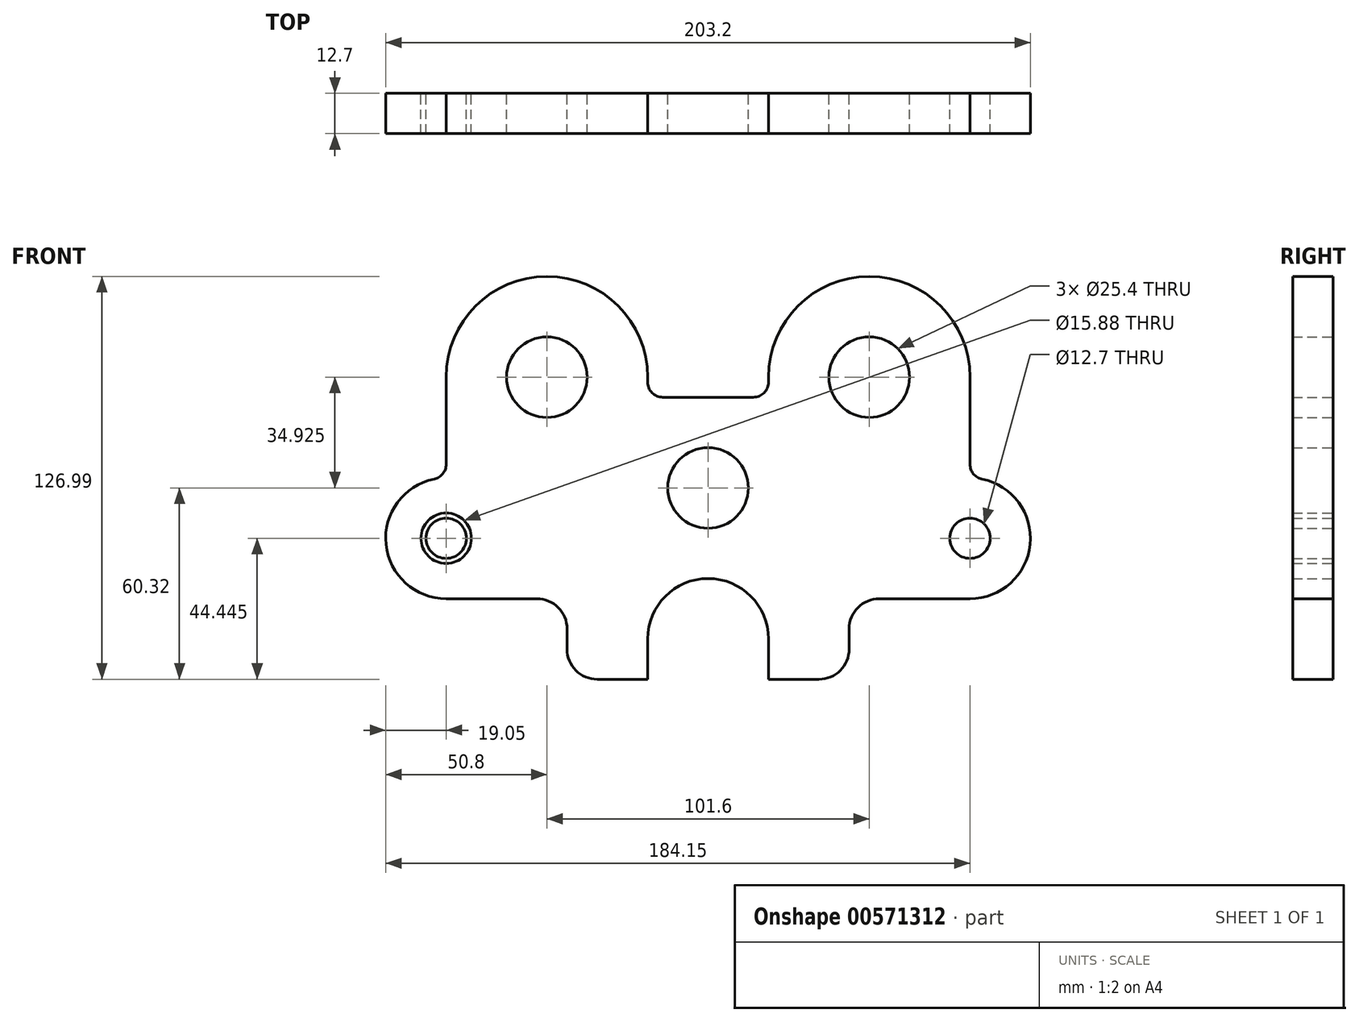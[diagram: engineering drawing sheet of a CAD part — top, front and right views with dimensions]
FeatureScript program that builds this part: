
annotation { "Feature Type Name" : "Feature", "Feature Type Description" : "" }
export const myFeature = defineFeature(function(context is Context, id is Id, definition is map)
    precondition{}
    {
        {
            var Q0;
            Q0=qCreatedBy(makeId("Front.planeOp"),FACE);
            var sketch = newSketch(context, id + "F0", { "sketchPlane" : qUnion([Q0])});
            skLineSegment(sketch, "E0", {"start": v(0, 76.7) * mm, "end": v(0, -75.9) * mm, "construction": true});
            skLineSegment(sketch, "E1", {"start": v(50.8, 76.08) * mm, "end": v(50.8, 12.52) * mm, "construction": true});
            skCircle(sketch, "E2", {"center": v(0, 0) * mm, "radius": 12.7 * mm});
            skCircle(sketch, "E3", {"center": v(50.8, 34.93) * mm, "radius": 12.7 * mm});
            skLineSegment(sketch, "E4", {"start": v(0, 28.58) * mm, "end": v(14.29, 28.58) * mm});
            skArc(sketch, "E5", {"start": v(82.55, 34.93) * mm, "mid": v(50.8, 66.68) * mm, "end": v(19.05, 34.93) * mm});
            skPoint(sketch, "E6.visualSharp", {"position": v(19.7, 28.58) * mm});
            skLineSegment(sketch, "E7", {"start": v(82.55, -34.92) * mm, "end": v(53.98, -34.92) * mm});
            skLineSegment(sketch, "E8", {"start": v(-29.42, 0) * mm, "end": v(25.25, 0) * mm, "construction": true});
            skCircle(sketch, "E9", {"center": v(82.55, -15.87) * mm, "radius": 6.35 * mm});
            skLineSegment(sketch, "E10", {"start": v(19.05, 34.93) * mm, "end": v(19.05, 33.34) * mm});
            skLineSegment(sketch, "E11", {"start": v(82.55, -7.94) * mm, "end": v(82.55, -31.6) * mm, "construction": true});
            skLineSegment(sketch, "E12", {"start": v(82.55, 34.93) * mm, "end": v(82.55, 7.46) * mm});
            skLineSegment(sketch, "E13", {"start": v(22.13, 34.93) * mm, "end": v(67.82, 34.93) * mm, "construction": true});
            skLineSegment(sketch, "E14", {"start": v(59.23, -15.87) * mm, "end": v(95.93, -15.87) * mm, "construction": true});
            skLineSegment(sketch, "E15", {"start": v(44.45, -44.45) * mm, "end": v(44.45, -50.8) * mm});
            skLineSegment(sketch, "E16", {"start": v(34.93, -60.32) * mm, "end": v(19.05, -60.32) * mm});
            skLineSegment(sketch, "E17", {"start": v(19.05, -60.32) * mm, "end": v(19.05, -47.62) * mm});
            skLineSegment(sketch, "E18.MirrorCS", {"start": v(0, 28.58) * mm, "end": v(-14.29, 28.58) * mm});
            skLineSegment(sketch, "E19.MirrorCS", {"start": v(-19.05, 34.93) * mm, "end": v(-19.05, 33.34) * mm});
            skArc(sketch, "E20.MirrorCS", {"start": v(-82.55, 34.93) * mm, "mid": v(-50.8, 66.68) * mm, "end": v(-19.05, 34.93) * mm});
            skLineSegment(sketch, "E21.MirrorCS", {"start": v(-82.55, 34.93) * mm, "end": v(-82.55, 7.46) * mm});
            skArc(sketch, "E22.MirrorCS", {"start": v(-82.55, -34.93) * mm, "mid": v(-101.5, -17.79) * mm, "end": v(-86.36, 2.8) * mm});
            skLineSegment(sketch, "E23.MirrorCS", {"start": v(-82.55, -34.93) * mm, "end": v(-53.97, -34.93) * mm});
            skLineSegment(sketch, "E24.MirrorCS", {"start": v(-44.45, -44.45) * mm, "end": v(-44.45, -50.8) * mm});
            skLineSegment(sketch, "E25.MirrorCS", {"start": v(-34.92, -60.32) * mm, "end": v(-19.05, -60.32) * mm});
            skLineSegment(sketch, "E26.MirrorCS", {"start": v(-19.05, -60.32) * mm, "end": v(-19.05, -47.62) * mm});
            skCircle(sketch, "E27.MirrorC", {"center": v(-50.8, 34.93) * mm, "radius": 12.7 * mm});
            skCircle(sketch, "E28.MirrorC", {"center": v(-82.55, -15.88) * mm, "radius": 6.35 * mm});
            skLineSegment(sketch, "E29.MirrorCS", {"start": v(-59.23, -15.87) * mm, "end": v(-95.93, -15.87) * mm, "construction": true});
            skLineSegment(sketch, "E30.MirrorCS", {"start": v(-82.55, -7.94) * mm, "end": v(-82.55, -31.6) * mm, "construction": true});
            skLineSegment(sketch, "E31.MirrorCS", {"start": v(-50.8, 76.08) * mm, "end": v(-50.8, 12.52) * mm, "construction": true});
            skLineSegment(sketch, "E32.MirrorCS", {"start": v(-22.13, 34.93) * mm, "end": v(-67.82, 34.93) * mm, "construction": true});
            skArc(sketch, "E33", {"start": v(19.05, -47.62) * mm, "mid": v(0, -28.57) * mm, "end": v(-19.05, -47.62) * mm});
            skPoint(sketch, "E34.visualSharp", {"position": v(-44.45, -34.92) * mm});
            skArc(sketch, "E34.filletArc", {"start": v(-44.45, -44.45) * mm, "mid": v(-47.24, -37.71) * mm, "end": v(-53.97, -34.93) * mm});
            skPoint(sketch, "E35.visualSharp", {"position": v(44.45, -34.92) * mm});
            skArc(sketch, "E35.filletArc", {"start": v(53.98, -34.92) * mm, "mid": v(47.24, -37.71) * mm, "end": v(44.45, -44.45) * mm});
            skPoint(sketch, "E36.visualSharp", {"position": v(44.45, -60.32) * mm});
            skArc(sketch, "E36.filletArc", {"start": v(34.93, -60.32) * mm, "mid": v(41.66, -57.54) * mm, "end": v(44.45, -50.8) * mm});
            skPoint(sketch, "E37.visualSharp", {"position": v(-44.45, -60.32) * mm});
            skArc(sketch, "E37.filletArc", {"start": v(-44.45, -50.8) * mm, "mid": v(-41.66, -57.54) * mm, "end": v(-34.92, -60.32) * mm});
            skLineSegment(sketch, "E38", {"start": v(0, -47.62) * mm, "end": v(26.3, -47.62) * mm, "construction": true});
            skLineSegment(sketch, "E39", {"start": v(26.3, -47.62) * mm, "end": v(-26.62, -47.62) * mm, "construction": true});
            skPoint(sketch, "E40.visualSharp", {"position": v(-82.55, 3.17) * mm});
            skArc(sketch, "E40.filletArc", {"start": v(-86.36, 2.8) * mm, "mid": v(-83.62, 4.44) * mm, "end": v(-82.55, 7.46) * mm});
            skArc(sketch, "E41.MirrorCS", {"start": v(82.55, -34.92) * mm, "mid": v(101.5, -17.79) * mm, "end": v(86.36, 2.8) * mm});
            skPoint(sketch, "E42.MirrorP", {"position": v(82.55, 3.18) * mm});
            skArc(sketch, "E43.MirrorCS", {"start": v(86.36, 2.8) * mm, "mid": v(83.62, 4.44) * mm, "end": v(82.55, 7.46) * mm});
            skPoint(sketch, "E44.visualSharp", {"position": v(-19.05, 28.57) * mm});
            skArc(sketch, "E44.filletArc", {"start": v(-19.05, 33.34) * mm, "mid": v(-17.66, 29.97) * mm, "end": v(-14.29, 28.58) * mm});
            skPoint(sketch, "E45.visualSharp", {"position": v(19.05, 28.58) * mm});
            skArc(sketch, "E45.filletArc", {"start": v(14.29, 28.58) * mm, "mid": v(17.66, 29.97) * mm, "end": v(19.05, 33.34) * mm});
            skCircle(sketch, "E46", {"center": v(82.55, -15.87) * mm, "radius": 7.94 * mm});
            skCircle(sketch, "E47", {"center": v(-82.55, -15.88) * mm, "radius": 7.94 * mm});
            skSolve(sketch);
        }
        {
            var Q0;
            Q0=qSketchRegion(id+"F0",true);
            var Q1;
            Q1=makeQuery(id+"F0.imprint","IMPRINT",FACE,{"disambiguationData":[TD([[makeQuery(id+"F0.imprint","IMPRINT",EDGE,{"derivedFrom":sQuery(id+"F0.wireOp",EDGE,"E9")}),-1.0]])]});
            var Q2;
            Q2=makeQuery(id+"F0.imprint","IMPRINT",FACE,{"disambiguationData":[TD([[makeQuery(id+"F0.imprint","IMPRINT",EDGE,{"derivedFrom":sQuery(id+"F0.wireOp",EDGE,"E28.MirrorC")}),1.0]])]});
            extrude(context, id + "F1", {"entities" : qUnion([Q0, Q1, Q2]), "endBound" : BoundingType.SYMMETRIC, "depth" : 12.7 * mm, "offsetDistance" : 25.4 * mm});
        }
    });
